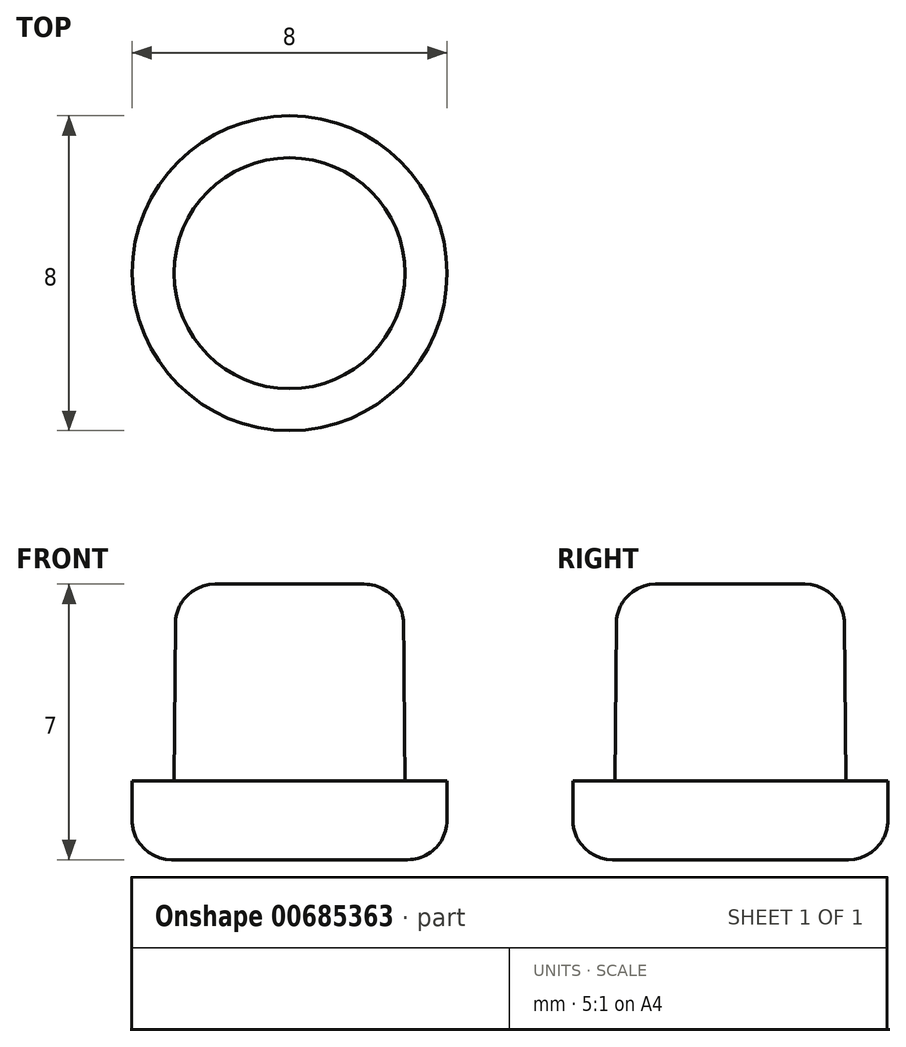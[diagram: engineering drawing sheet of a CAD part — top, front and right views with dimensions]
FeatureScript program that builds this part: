
annotation { "Feature Type Name" : "Feature", "Feature Type Description" : "" }
export const myFeature = defineFeature(function(context is Context, id is Id, definition is map)
    precondition{}
    {
        {
            var Q0;
            Q0=qCreatedBy(makeId("Top.planeOp"),FACE);
            var sketch = newSketch(context, id + "F0", { "sketchPlane" : qUnion([Q0])});
            skCircle(sketch, "E0", {"center": v(0, 0) * mm, "radius": 2.95 * mm});
            skCircle(sketch, "E1", {"center": v(0, 0) * mm, "radius": 4 * mm});
            skSolve(sketch);
        }
        {
            var Q0;
            Q0=makeQuery(id+"F0.imprint","IMPRINT",FACE,{"disambiguationData":[TD([[makeQuery(id+"F0.imprint","IMPRINT",EDGE,{"derivedFrom":sQuery(id+"F0.wireOp",EDGE,"E0")}),1.0]])]});
            extrude(context, id + "F1", {"entities" : qUnion([Q0]), "depth" : 7 * mm, "offsetDistance" : 25 * mm, "hasDraft" : true, "draftAngle" : .5 * degree, "draftPullDirection" : true});
        }
        {
            var Q0;
            Q0=makeQuery(id+"F0.imprint","IMPRINT",FACE,{"disambiguationData":[TD([[makeQuery(id+"F0.imprint","IMPRINT",EDGE,{"derivedFrom":sQuery(id+"F0.wireOp",EDGE,"E0")}),-1.0]])]});
            var Q1;
            Q1=makeQuery(id+"F0.imprint","IMPRINT",FACE,{"disambiguationData":[TD([[makeQuery(id+"F0.imprint","IMPRINT",EDGE,{"derivedFrom":sQuery(id+"F0.wireOp",EDGE,"E0")}),1.0]])]});
            extrude(context, id + "F2", {"entities" : qUnion([Q0, Q1]), "operationType" : NewBodyOperationType.ADD, "depth" : 2 * mm, "offsetDistance" : 25 * mm});
        }
        {
            var Q0;
            Q0=makeQuery(id+"F2.opExtrude","CAP_EDGE",EDGE,{"disambiguationData":[OSD([sQuery(id+"F0.wireOp",EDGE,"E1")])],"isStart":true});
            var Q1;
            Q1=makeQuery(id+"F1.opExtrude","CAP_EDGE",EDGE,{"disambiguationData":[OSD([sQuery(id+"F0.wireOp",EDGE,"E0")])],"isStart":false});
            fillet(context, id + "F3", {"entities" : qUnion([Q0, Q1]), "radius" : 1 * mm, "tangentPropagation" : true, "allowEdgeOverflow" : false});
        }
    });
